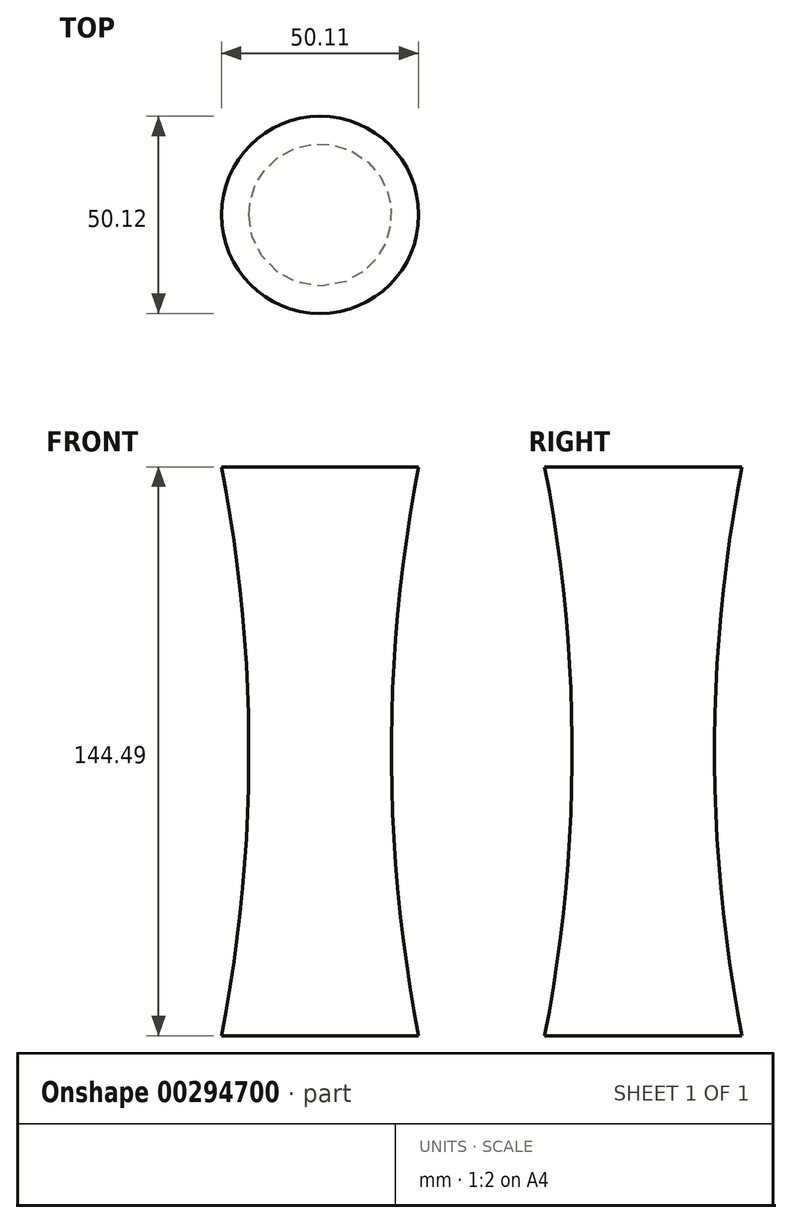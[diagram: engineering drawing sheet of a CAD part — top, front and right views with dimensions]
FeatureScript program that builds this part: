
annotation { "Feature Type Name" : "Feature", "Feature Type Description" : "" }
export const myFeature = defineFeature(function(context is Context, id is Id, definition is map)
    precondition{}
    {
        {
            var Q0;
            Q0=qCreatedBy(makeId("Front.planeOp"),FACE);
            var sketch = newSketch(context, id + "F0", { "sketchPlane" : qUnion([Q0])});
            skLineSegment(sketch, "E0.bottom", {"start": v(-16.41, -40.59) * mm, "end": v(33.7, -40.59) * mm});
            skLineSegment(sketch, "E0.top", {"start": v(-16.41, 103.9) * mm, "end": v(33.7, 103.9) * mm});
            skLineSegment(sketch, "E0.left", {"start": v(-16.41, -40.59) * mm, "end": v(-16.41, 103.9) * mm});
            skLineSegment(sketch, "E0.right", {"start": v(33.7, -40.59) * mm, "end": v(33.7, 103.9) * mm});
            skArc(sketch, "E1", {"start": v(-16.41, -40.59) * mm, "mid": v(-9.47, 31.65) * mm, "end": v(-16.41, 103.9) * mm});
            skArc(sketch, "E2", {"start": v(33.7, 103.9) * mm, "mid": v(27.65, 31.65) * mm, "end": v(33.7, -40.59) * mm});
            skLineSegment(sketch, "E3", {"start": v(8.65, -40.59) * mm, "end": v(8.65, 103.9) * mm});
            skSolve(sketch);
        }
        {
            var Q0;
            {var subQ0=sQuery(id+"F0.wireOp",EDGE,"E1");Q0=makeQuery(id+"F0.imprint","IMPRINT",FACE,{"disambiguationData":[TD([[makeQuery(id+"F0.imprint","IMPRINT",EDGE,{"derivedFrom":subQ0}),-1.0]])]});}
            var Q1;
            Q1=sQuery(id+"F0.wireOp",EDGE,"E1");
            var Q2;
            Q2=sQuery(id+"F0.wireOp",EDGE,"E3");
            revolve(context, id + "F1", {"entities" : qUnion([Q0]), "surfaceEntities" : qUnion([Q1]), "axis" : qUnion([Q2]), "revolveType" : RevolveType.FULL});
        }
    });
